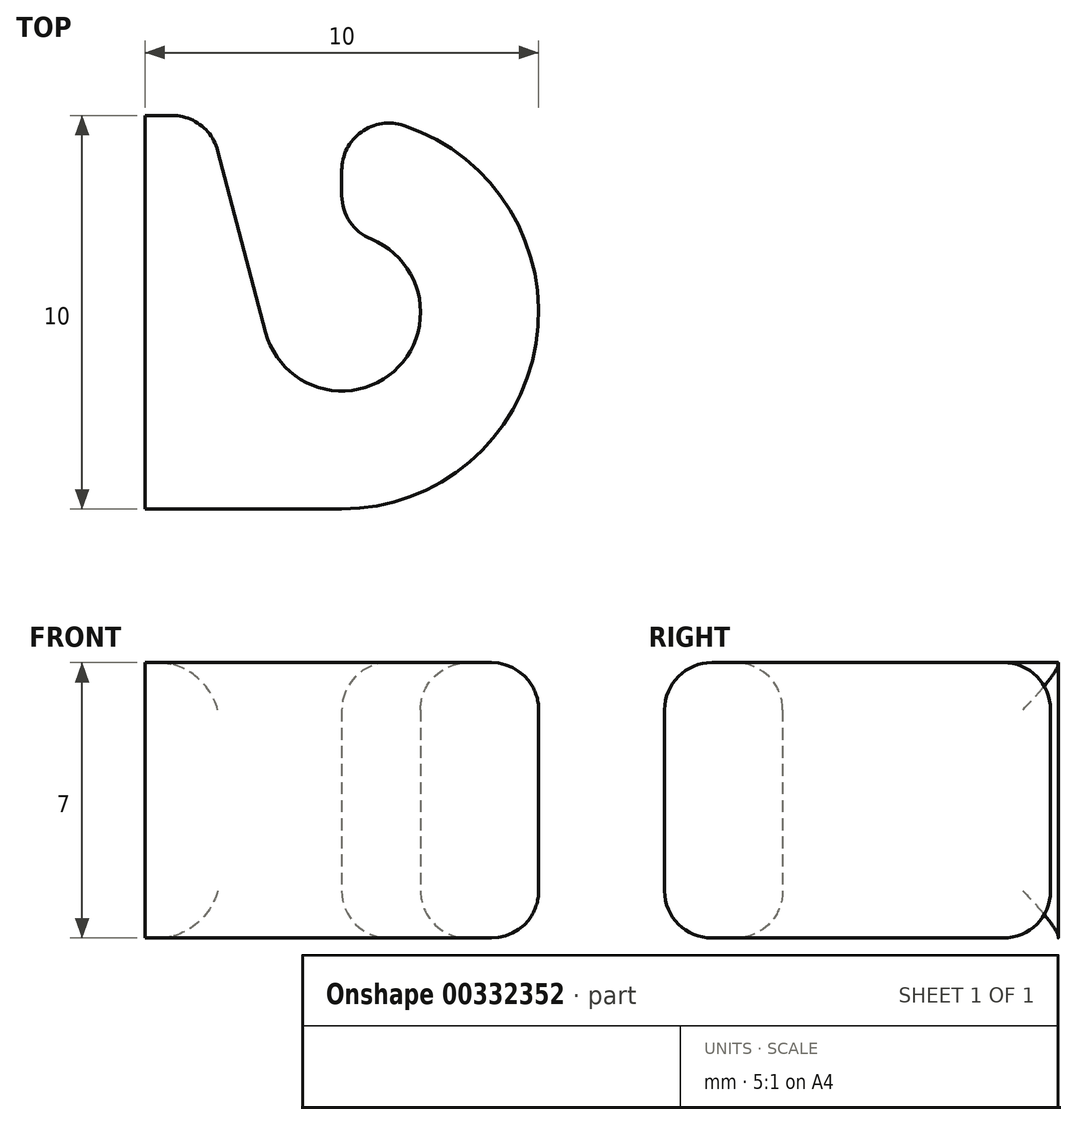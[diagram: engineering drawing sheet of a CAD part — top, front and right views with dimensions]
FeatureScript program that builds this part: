
annotation { "Feature Type Name" : "Feature", "Feature Type Description" : "" }
export const myFeature = defineFeature(function(context is Context, id is Id, definition is map)
    precondition{}
    {
        {
            var Q0;
            Q0=qCreatedBy(makeId("Top.planeOp"),FACE);
            var sketch = newSketch(context, id + "F0", { "sketchPlane" : qUnion([Q0])});
            skCircle(sketch, "E0", {"center": v(0, 0) * mm, "radius": 5 * mm});
            skCircle(sketch, "E1", {"center": v(0, 0) * mm, "radius": 2 * mm});
            skLineSegment(sketch, "E2", {"start": v(0, -5) * mm, "end": v(-5, -5) * mm});
            skLineSegment(sketch, "E3", {"start": v(-5, -5) * mm, "end": v(-5, 0) * mm});
            skLineSegment(sketch, "E4", {"start": v(0, 5) * mm, "end": v(0, 2) * mm});
            skLineSegment(sketch, "E5", {"start": v(-5, 0) * mm, "end": v(-5, 5) * mm});
            skLineSegment(sketch, "E6", {"start": v(-5, 5) * mm, "end": v(0, 5) * mm});
            skLineSegment(sketch, "E7", {"start": v(-3.39, 5) * mm, "end": v(-1.93, -0.51) * mm});
            skSolve(sketch);
        }
        {
            var Q0;
            {var subQ0=sQuery(id+"F0.wireOp",EDGE,"EHWh9kV6-72sz-qOpt-SCcs-0i8UYRI7YqYi");Q0=makeQuery(id+"F0.imprint","IMPRINT",FACE,{"disambiguationData":[TD([[makeQuery(id+"F0.imprint","IMPRINT",EDGE,{"derivedFrom":subQ0}),-1.0]])]});}
            var Q1;
            {var subQ0=sQuery(id+"F0.wireOp",EDGE,"E2");Q1=makeQuery(id+"F0.imprint","IMPRINT",FACE,{"disambiguationData":[TD([[makeQuery(id+"F0.imprint","IMPRINT",EDGE,{"derivedFrom":subQ0}),-1.0]])]});}
            var Q2;
            {var subQ0=sQuery(id+"F0.wireOp",EDGE,"E4");Q2=makeQuery(id+"F0.imprint","IMPRINT",FACE,{"disambiguationData":[TD([[makeQuery(id+"F0.imprint","IMPRINT",EDGE,{"derivedFrom":subQ0}),1.0]])]});}
            var Q3;
            {var subQ0=sQuery(id+"F0.wireOp",EDGE,"E5");Q3=makeQuery(id+"F0.imprint","IMPRINT",FACE,{"disambiguationData":[TD([[makeQuery(id+"F0.imprint","IMPRINT",EDGE,{"derivedFrom":subQ0}),-1.0]])]});}
            extrude(context, id + "F1", {"entities" : qUnion([Q0, Q1, Q2, Q3]), "depth" : 7 * mm});
        }
        {
            var Q0;
            Q0=makeQuery(id+"F1.opExtrude","CAP_EDGE",EDGE,{"disambiguationData":[OSD([sQuery(id+"F0.wireOp",EDGE,"E1")])],"isStart":true});
            var Q1;
            Q1=makeQuery(id+"F1.opExtrude","CAP_EDGE",EDGE,{"disambiguationData":[OSD([sQuery(id+"F0.wireOp",EDGE,"E1")])],"isStart":false});
            var Q2;
            Q2=makeQuery(id+"F1.opExtrude","CAP_EDGE",EDGE,{"disambiguationData":[OSD([sQuery(id+"F0.wireOp",EDGE,"E0")])],"isStart":true});
            var Q3;
            Q3=makeQuery(id+"F1.opExtrude","CAP_EDGE",EDGE,{"disambiguationData":[OSD([sQuery(id+"F0.wireOp",EDGE,"E0")])],"isStart":false});
            var Q4;
            Q4=makeQuery(id+"F1.opExtrude","SWEPT_EDGE",EDGE,{"disambiguationData":[OSD([sQuery(id+"F0.wireOp",EDGE,"E1"),sQuery(id+"F0.wireOp",EDGE,"EHWh9kV6-72sz-qOpt-SCcs-0i8UYRI7YqYi")])]});
            var Q5;
            Q5=makeQuery(id+"F1.opExtrude","CAP_EDGE",EDGE,{"disambiguationData":[OSD([sQuery(id+"F0.wireOp",EDGE,"EHWh9kV6-72sz-qOpt-SCcs-0i8UYRI7YqYi")])],"isStart":false});
            var Q6;
            Q6=makeQuery(id+"F1.opExtrude","CAP_EDGE",EDGE,{"disambiguationData":[OSD([sQuery(id+"F0.wireOp",EDGE,"EHWh9kV6-72sz-qOpt-SCcs-0i8UYRI7YqYi")])],"isStart":true});
            var Q7;
            Q7=makeQuery(id+"F1.opExtrude","SWEPT_EDGE",EDGE,{"disambiguationData":[OSD([sQuery(id+"F0.wireOp",EDGE,"E0"),sQuery(id+"F0.wireOp",EDGE,"E4")])]});
            var Q8;
            Q8=makeQuery(id+"F1.opExtrude","SWEPT_EDGE",EDGE,{"disambiguationData":[OSD([sQuery(id+"F0.wireOp",EDGE,"E1"),sQuery(id+"F0.wireOp",EDGE,"E4")])]});
            var Q9;
            Q9=makeQuery(id+"F1.opExtrude","CAP_EDGE",EDGE,{"disambiguationData":[OSD([sQuery(id+"F0.wireOp",EDGE,"E4")])],"isStart":false});
            var Q10;
            Q10=makeQuery(id+"F1.opExtrude","CAP_EDGE",EDGE,{"disambiguationData":[OSD([sQuery(id+"F0.wireOp",EDGE,"E4")])],"isStart":true});
            var Q11;
            Q11=makeQuery(id+"F1.opExtrude","SWEPT_EDGE",EDGE,{"disambiguationData":[OSD([sQuery(id+"F0.wireOp",EDGE,"E6"),sQuery(id+"F0.wireOp",EDGE,"E7")])]});
            fillet(context, id + "F2", {"entities" : qUnion([Q0, Q1, Q2, Q3, Q4, Q5, Q6, Q7, Q8, Q9, Q10, Q11]), "radius" : 1.2 * mm, "tangentPropagation" : true, "allowEdgeOverflow" : false});
        }
    });
